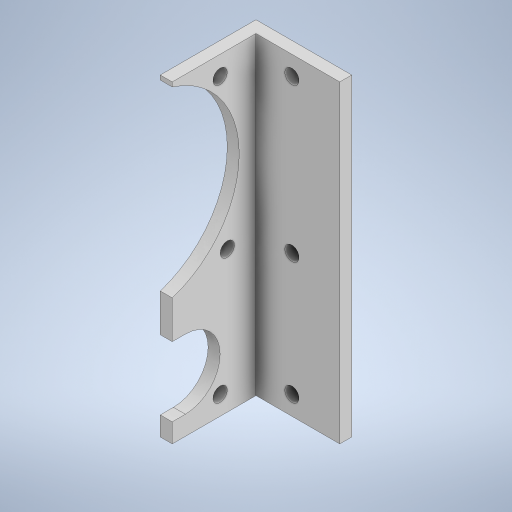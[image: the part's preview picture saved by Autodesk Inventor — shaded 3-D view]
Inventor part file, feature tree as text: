
AUTODESK INVENTOR PART (.ipt)
format: ipt  version: 2023 (Build 270158000, 158)  size: 282,624 bytes
history: native  units: in
note: dims shown in document units (in); Inventor stores cm internally (conversion verified against a paired STEP export)
features: extrude x3, mirror x1, sketch x1
ambient origin geometry x8: Origin, YZ Plane, XZ Plane, XY Plane, X Axis, Y Axis, Z Axis, Center Point
bodies: Solid2 (feature_tree)
feature tree (5):
  extrude  "Extrusion3"  Depth=0.125in
  extrude  "Extrusion4"  Depth=0.125in TaperAngle=0.0deg
  extrude  "Extrusion5"  Depth=1.0in TaperAngle=0.0deg
  mirror  "Mirror1"
  sketch  "Sketch3"  dims[d16=0.15in d41=0.125in d42=0.125in d43=0.0in d44=1.0in d45=0.0in d46=0.15in d47=0.15in d48=0.15in d49=1.0in d50=0.0in d51=0.15in d52=0.15in]
